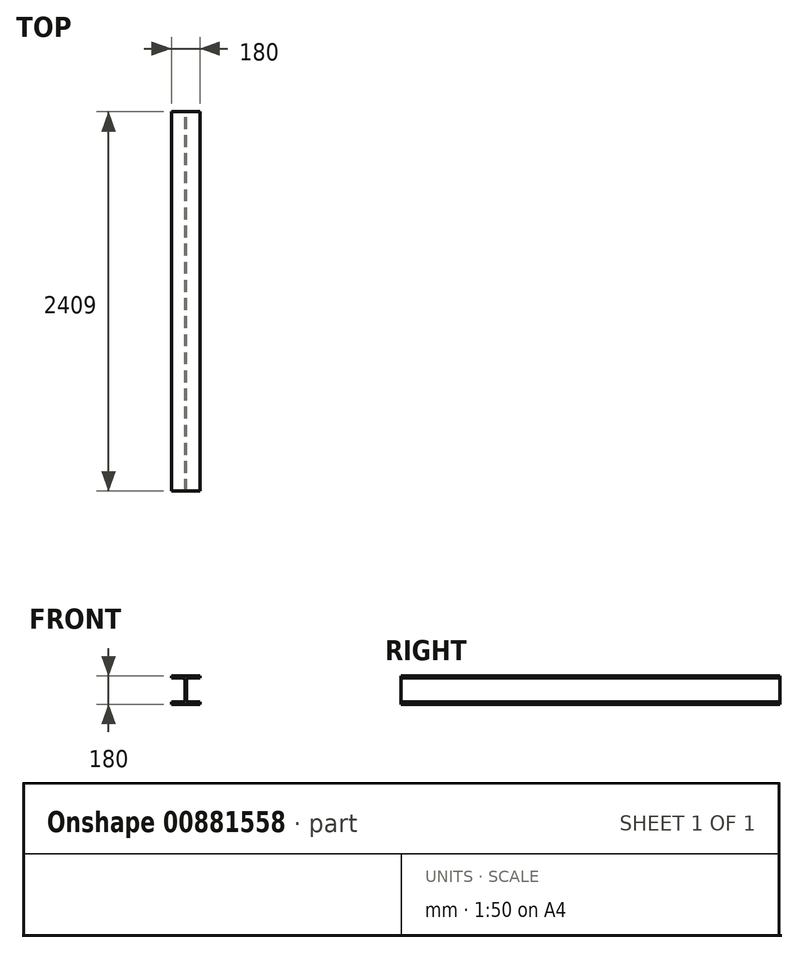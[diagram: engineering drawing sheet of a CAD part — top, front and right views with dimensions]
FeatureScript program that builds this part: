
annotation { "Feature Type Name" : "Feature", "Feature Type Description" : "" }
export const myFeature = defineFeature(function(context is Context, id is Id, definition is map)
    precondition{}
    {
        {
            var Q0;
            Q0=qCreatedBy(makeId("Front.planeOp"),FACE);
            var sketch = newSketch(context, id + "F0", { "sketchPlane" : qUnion([Q0])});
            skLineSegment(sketch, "E0.bottom", {"start": v(90, -90) * mm, "end": v(-90, -90) * mm});
            skLineSegment(sketch, "E0.top", {"start": v(90, 90) * mm, "end": v(-90, 90) * mm});
            skLineSegment(sketch, "E0.left", {"start": v(90, -90) * mm, "end": v(90, -76) * mm});
            skLineSegment(sketch, "E0.right", {"start": v(-90, -90) * mm, "end": v(-90, -76) * mm});
            skPoint(sketch, "E0.middle", {"position": v(0, 0) * mm});
            skLineSegment(sketch, "E1.bottom", {"start": v(-90, 76) * mm, "end": v(-19.25, 76) * mm});
            skLineSegment(sketch, "E1.top", {"start": v(-90, -76) * mm, "end": v(-19.25, -76) * mm});
            skLineSegment(sketch, "E1.right", {"start": v(-4.25, 61) * mm, "end": v(-4.25, -61) * mm});
            skLineSegment(sketch, "E2.bottom", {"start": v(90, 76) * mm, "end": v(19.25, 76) * mm});
            skLineSegment(sketch, "E2.top", {"start": v(90, -76) * mm, "end": v(19.25, -76) * mm});
            skLineSegment(sketch, "E2.right", {"start": v(4.25, 61) * mm, "end": v(4.25, -61) * mm});
            skPoint(sketch, "E3.visualSharp", {"position": v(4.25, 76) * mm});
            skArc(sketch, "E3.filletArc", {"start": v(19.25, 76) * mm, "mid": v(8.64, 71.6) * mm, "end": v(4.25, 61) * mm});
            skPoint(sketch, "E4.visualSharp", {"position": v(4.25, -76) * mm});
            skArc(sketch, "E4.filletArc", {"start": v(4.25, -61) * mm, "mid": v(8.64, -71.6) * mm, "end": v(19.25, -76) * mm});
            skPoint(sketch, "E5.visualSharp", {"position": v(-4.25, -76) * mm});
            skArc(sketch, "E5.filletArc", {"start": v(-19.25, -76) * mm, "mid": v(-8.64, -71.6) * mm, "end": v(-4.25, -61) * mm});
            skPoint(sketch, "E6.visualSharp", {"position": v(-4.25, 76) * mm});
            skArc(sketch, "E6.filletArc", {"start": v(-4.25, 61) * mm, "mid": v(-8.64, 71.6) * mm, "end": v(-19.25, 76) * mm});
            skLineSegment(sketch, "E7.trimOffspring", {"start": v(-90, 76) * mm, "end": v(-90, 90) * mm});
            skLineSegment(sketch, "E8.trimOffspring", {"start": v(90, 76) * mm, "end": v(90, 90) * mm});
            skSolve(sketch);
        }
        {
            var Q0;
            Q0 = qSketchRegion(id + "F0", true);
            extrude(context, id + "F1", {"entities" : qUnion([Q0]), "depth" : 2409 * mm, "offsetDistance" : 25 * mm});
        }
    });
